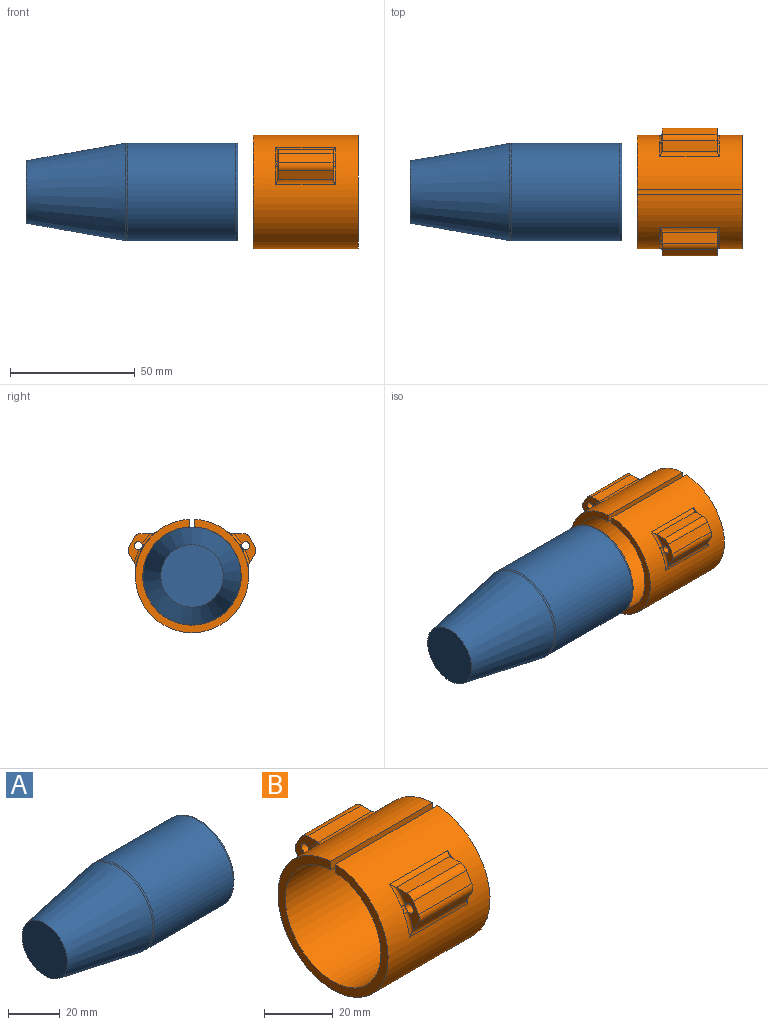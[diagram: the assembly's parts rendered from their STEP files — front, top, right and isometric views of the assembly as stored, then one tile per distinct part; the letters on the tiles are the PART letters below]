
ASSEMBLY  parts=2 mates=1
PART A: 9 faces, bbox 84.9x42.4x42.4 mm
  f0: cylinder r=19.6mm len=43.2mm, axis (1,0,0), area 5319.7mm2, adj f5,f8
  f1: plane 37.2x37.2mm, normal (1,0,0), area 124.8mm2, adj f4,f5
  f2: cylinder r=16.5mm len=33mm, axis (1,0,0), area 725.7mm2, adj f3,f4
  f3: plane 33x33mm, normal (1,0,0), area 855.3mm2, adj f2
  f4: torus R=17.5mm, axis (1,0,0), area 166.4mm2, adj f1,f2
  f5: torus R=18.6mm, axis (1,0,0), area 189.9mm2, adj f0,f1
  f6: cone r=12.5mm half-angle=10deg, axis (1,0,0), area 4069.5mm2, adj f7,f8
  f7: plane 25x25mm, normal (-1,0,0), area 490.9mm2, adj f6
  f8: torus R=14.6mm, axis (1,0,0), area 107.3mm2, adj f0,f6
PART B: 39 faces, bbox 42x51.2x45.4 mm
  f0: plane 45.4x45.38mm, normal (1,0,0), area 393.6mm2, adj f1,f2,f3,f4
  f1: cylinder r=22.7mm len=45.4mm, axis (1,0,0), area 5491.5mm2, adj f0,f2,f4,f5,f6,f7,f8,f9
  f2: plane 42x3mm, normal (0,-1,0), area 126.1mm2, adj f0,f1,f3,f5
  f3: cylinder r=19.7mm len=42mm, axis (1,0,0), area 5114.7mm2, adj f0,f2,f4,f5
  f4: plane 42x3mm, normal (0,1,0), area 126.1mm2, adj f0,f1,f3,f5
  f5: plane 45.4x45.38mm, normal (-1,0,0), area 393.6mm2, adj f1,f2,f3,f4
  f6: cylinder r=3mm len=24mm, axis (1,0,0), area 45.2mm2, adj f1,f7,f13,f14
  f7: torus R=23.7mm, axis (-1,0,0), area 10.3mm2, adj f1,f6,f8,f14,f15
  f8: bspline ~2.79x2.24mm, area 2.7mm2, adj f1,f7,f9,f16
  f9: torus R=23.7mm, axis (-1,0,0), area 10.1mm2, adj f1,f8,f10,f15,f17
  f10: cylinder r=3mm len=24mm, axis (1,0,0), area 46.9mm2, adj f1,f9,f11,f17
  f11: torus R=23.7mm, axis (1,0,0), area 10.1mm2, adj f1,f10,f12,f17,f18
  f12: bspline ~2.85x2.23mm, area 2.7mm2, adj f1,f11,f13,f16
  f13: torus R=23.7mm, axis (1,0,0), area 10.3mm2, adj f1,f6,f12,f14,f18
  f14: plane 22.1x3.97mm, normal (0,-0.87,-0.5), area 100.9mm2, adj f6,f7,f13,f15,f18,f19
  f15: plane 11.78x9.07mm, normal (-1,0,0), area 36.1mm2, adj f7,f9,f14,f16,f17,f19,f20,f21
  f16: cylinder r=1.6mm len=22mm, axis (1,0,0), area 221.2mm2, adj f8,f12,f15,f18
  f17: plane 22.07x4.3mm, normal (0,0,1), area 94.6mm2, adj f9,f10,f11,f15,f18,f21
  f18: plane 11.78x9.07mm, normal (1,0,0), area 36.1mm2, adj f11,f13,f14,f16,f17,f19,f20,f21
  f19: cylinder r=3mm len=22mm, axis (1,0,0), area 69.1mm2, adj f14,f15,f18,f20
  f20: plane 22x3.71mm, normal (0,-0.87,0.5), area 94.3mm2, adj f15,f18,f19,f21
  f21: cylinder r=3mm len=22mm, axis (1,0,0), area 69.1mm2, adj f15,f17,f18,f20
  f22: plane 22.07x4.3mm, normal (0,0,1), area 94.6mm2, adj f23,f24,f25,f26,f27,f28
  f23: plane 11.78x9.07mm, normal (-1,0,0), area 36.1mm2, adj f22,f24,f28,f29,f30,f31,f32,f33
  f24: torus R=23.7mm, axis (-1,0,0), area 10.1mm2, adj f22,f23,f25,f34,f35
  f25: cylinder r=3mm len=24mm, axis (1,0,0), area 46.9mm2, adj f22,f24,f26,f34
  f26: torus R=23.7mm, axis (1,0,0), area 10.1mm2, adj f22,f25,f27,f34,f36
  f27: plane 11.78x9.07mm, normal (1,0,0), area 36.1mm2, adj f22,f26,f28,f29,f31,f32,f33,f37
  f28: cylinder r=3mm len=22mm, axis (1,0,0), area 69.1mm2, adj f22,f23,f27,f32
  f29: plane 22.1x3.97mm, normal (0,0.87,-0.5), area 100.9mm2, adj f23,f27,f30,f33,f37,f38
  f30: torus R=23.7mm, axis (-1,0,0), area 10.3mm2, adj f23,f29,f34,f35,f38
  f31: cylinder r=1.6mm len=22mm, axis (1,0,0), area 221.2mm2, adj f23,f27,f35,f36
  f32: plane 22x3.71mm, normal (0,0.87,0.5), area 94.3mm2, adj f23,f27,f28,f33
  f33: cylinder r=3mm len=22mm, axis (1,0,0), area 69.1mm2, adj f23,f27,f29,f32
  f34: cylinder r=22.7mm len=24mm, axis (1,0,0), area 414.9mm2, adj f24,f25,f26,f30,f35,f36,f37,f38
  f35: bspline ~2.79x2.24mm, area 2.7mm2, adj f24,f30,f31,f34
  f36: bspline ~2.85x2.23mm, area 2.7mm2, adj f26,f31,f34,f37
  f37: torus R=23.7mm, axis (1,0,0), area 10.3mm2, adj f27,f29,f34,f36,f38
  f38: cylinder r=3mm len=24mm, axis (1,0,0), area 45.2mm2, adj f29,f30,f34,f37
PLACE A t=(33.73,6.51,-0.39)mm fixed
PLACE B t=(81.8,6.51,-0.39)mm
MATE slider B.f3 <-> A.f0  axis (1,0,0) through (81.8,6.51,-0.39)mm
